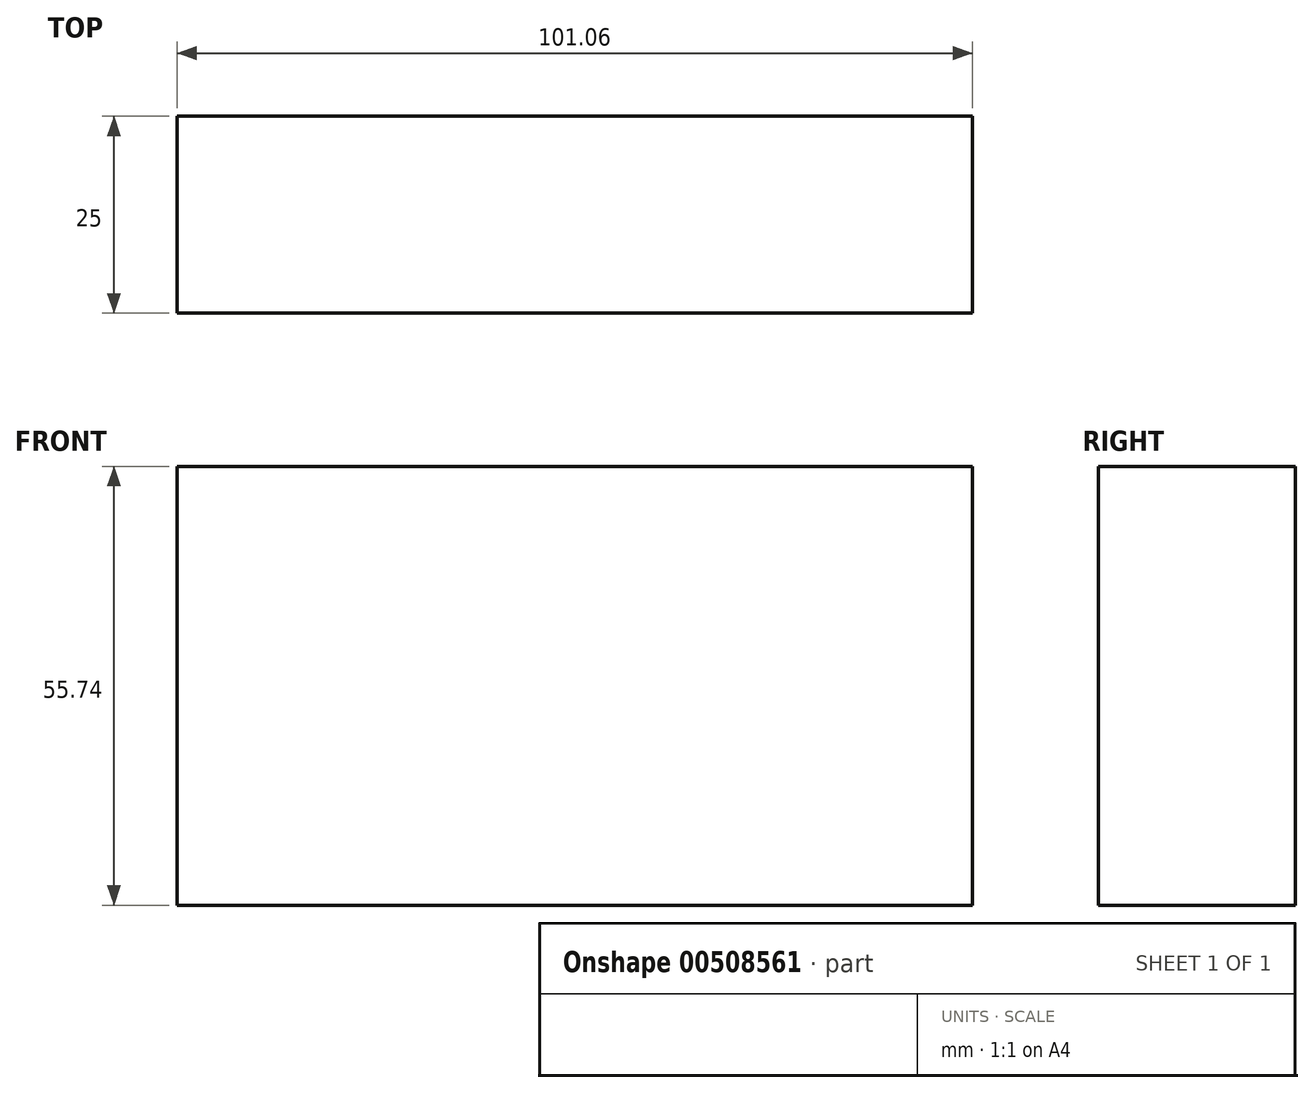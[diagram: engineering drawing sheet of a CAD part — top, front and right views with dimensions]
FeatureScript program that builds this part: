
annotation { "Feature Type Name" : "Feature", "Feature Type Description" : "" }
export const myFeature = defineFeature(function(context is Context, id is Id, definition is map)
    precondition{}
    {
        {
            var Q0;
            Q0=qCreatedBy(makeId("Front.planeOp"),FACE);
            var sketch = newSketch(context, id + "F0", { "sketchPlane" : qUnion([Q0])});
            skLineSegment(sketch, "E0.bottom", {"start": v(50.53, 27.87) * mm, "end": v(-50.53, 27.87) * mm});
            skLineSegment(sketch, "E0.top", {"start": v(50.53, -27.87) * mm, "end": v(-50.53, -27.87) * mm});
            skLineSegment(sketch, "E0.left", {"start": v(50.53, 27.87) * mm, "end": v(50.53, -27.87) * mm});
            skLineSegment(sketch, "E0.right", {"start": v(-50.53, 27.87) * mm, "end": v(-50.53, -27.87) * mm});
            skPoint(sketch, "E0.middle", {"position": v(0, 0) * mm});
            skSolve(sketch);
        }
        {
            var Q0;
            Q0 = qSketchRegion(id + "F0", true);
            extrude(context, id + "F1", {"entities" : qUnion([Q0]), "depth" : 25 * mm});
        }
    });
